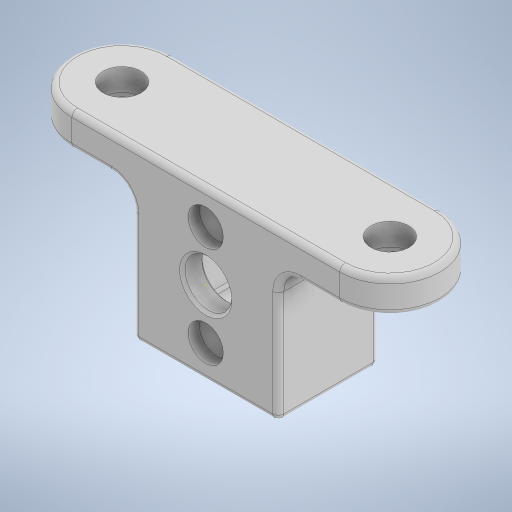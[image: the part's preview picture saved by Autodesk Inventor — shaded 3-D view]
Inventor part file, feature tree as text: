
AUTODESK INVENTOR PART (.ipt)
format: ipt  version: 2024.2 (Build 282272000, 272)  size: 385,024 bytes
history: native  units: mm
features: sketch x7, extrude x6, fillet x4, chamfer x1
ambient origin geometry x8: Origin, YZ Plane, XZ Plane, XY Plane, X Axis, Y Axis, Z Axis, Center Point
bodies: Solid1 (feature_tree)
feature tree (18):
  sketch  "Sketch1"  dims[d0=1.8mm d1=9.0mm]
  extrude  "Extrusion1"  Depth=9.0mm
  extrude  "Extrusion2"  Depth=4.5mm
  extrude  "Extrusion3"  Depth=15.0mm
  fillet  "Fillet1"  Radius=7.5mm
  fillet  "Fillet2"  Radius=6.5mm
  extrude  "Extrusion4"  Depth=1.5mm
  fillet  "Fillet3"  Radius=1.5mm
  fillet  "Fillet4"  Radius=1.5mm
  chamfer  "Chamfer1"  Distance=7.0mm
  extrude  "Extrusion5"  Depth=10.0mm
  extrude  "Extrusion6"  Depth=2.0mm
  sketch  "Sketch2"  dims[d2=4.195mm d3=4.5mm]
  sketch  "Sketch3"  dims[d4=13.0mm d5=15.0mm d6=7.5mm d7=6.5mm]
  sketch  "Sketch4"  dims[d8=2.0mm d9=0.0mm d10=1.5mm d11=1.5mm d12=1.5mm]
  sketch  "Sketch5"  dims[d13=1.5mm d14=7.0mm d15=0.0mm]
  sketch  "Sketch6"  dims[d16=3.4mm d17=10.0mm]
  sketch  "Sketch7"  dims[d18=3.0mm d19=0.0mm d20=2.0mm d21=4.5mm d22=4.5mm d23=4.5mm d24=5.25mm d25=1.0mm d26=0.0mm d27=0.5mm d28=0.25mm d29=2.0mm d30=45.0deg d31=0.25mm d32=3.15mm d33=1.0mm d34=0.0mm d35=0.2mm d36=0.0mm]
